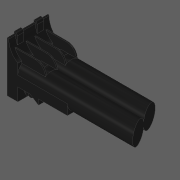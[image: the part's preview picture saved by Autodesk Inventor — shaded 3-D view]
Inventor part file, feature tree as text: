
AUTODESK INVENTOR PART (.ipt)
format: ipt  version: 2020 (Build 240168000, 168)  size: 1,102,848 bytes
history: native  units: in
note: dims shown in document units (in); Inventor stores cm internally (conversion verified against a paired STEP export)
features: other x33, extrude x19, loft x3, pattern_linear x3, fillet x2
ambient origin geometry x8: Origin, YZ Plane, XZ Plane, XY Plane, X Axis, Y Axis, Z Axis, Center Point
bodies: Body1 (feature_tree)
feature tree (60):
  other  "CrossSection1"
  other  "CrossSection2"
  other  "CrossSection3"
  other  "Whole"
  other  "Vertical Midplane"
  other  "Horizontal Midplane"
  extrude  "Block"  TaperAngle=0.0deg  [1 undecoded]
  extrude  "Hinge Protrusion"  Depth=0.7874in
  other  "Resonator Profile"
  extrude  "Resonator"  Depth=0.4724in
  extrude  "Resonator Cut"  Depth=0.3153in
  extrude  "Duct Cavity"  TaperAngle=0.0deg  [1 undecoded]
  other  "Duct Cavity Plane"
  loft  "Duct Entrance Loft"
  other  "Whistle Path Midplane"
  other  "Slit Loft To"
  loft  "Slit Loft"
  extrude  "Slit"  Depth=0.4882in
  other  "Fitting"
  extrude  "Edge Cut"  Depth=2.3498in
  other  "Edge Plane"
  other  "Edge Sketch"
  loft  "Edge Loft"
  extrude  "Edge"  Depth=0.1969in
  other  "Edge Cut Plane"
  extrude  "Spring Steel Slot"  Depth=0.1292in
  fillet  "Duct Fillet"  [1 undecoded]
  pattern_linear  "Channel Repetition"  Spacing1=0.2362in  [1 undecoded]
  extrude  "Edge Length Cut"  TaperAngle=0.0deg  [1 undecoded]
  other  "Tube Length Curve"
  extrude  "Tube Length Cut"  Depth=0.2441in
  extrude  "Whistle Walls"  Depth=0.1528in
  fillet  "Whistle Wall Fillet"  Radius=0.1245in
  pattern_linear  "Whistle Wall Repetition"  Spacing1=0.1528in  [1 undecoded]
  extrude  "End Caps"  Depth=0.2441in
  extrude  "Extra Block (for short notes)"  Depth=0.4921in
  other  "End Cap Tidying Plane"
  other  "End Cap Tidying Sketch"
  extrude  "End Cap Tidying"  Depth=0.0197in
  extrude  "End Cap Tidying (reverse)"  Depth=0.2559in
  pattern_linear  "End Cap Tidying Repetition"  Spacing1=0.8819in  [1 undecoded]
  extrude  "End Cap Tidying (edges)"  Depth=0.4882in
  extrude  "End Cap Tidying (edges, reverse)"  TaperAngle=0.0deg  [1 undecoded]
  other  "End-of-block Plane"
  extrude  "Manifold Slots"  Depth=0.2441in
  other  "Block Profile"
  other  "Fitting Sketch"
  other  "Duct Cavity Profile"
  other  "Duct Entrance Loft From"
  other  "Hinge Protrusion Sketch"
  other  "Edge Cut Sketch"
  other  "Edges3"
  other  "Edge Length Curve"
  other  "Whistle Wall Sketch"
  other  "2D Equation Curve10"
  other  "2D Equation Curve11"
  other  "Duct Entrance Loft To"
  other  "Slit Loft From"
  other  "Manifold Slot Sketch"
  other  "Spring Steel Slot Sketch"
note: 8 required parameter values undecoded (feature->parameter linkage not recoverable at this tier; creation-order binding heuristic only, values carry confidence <= 0.55)
